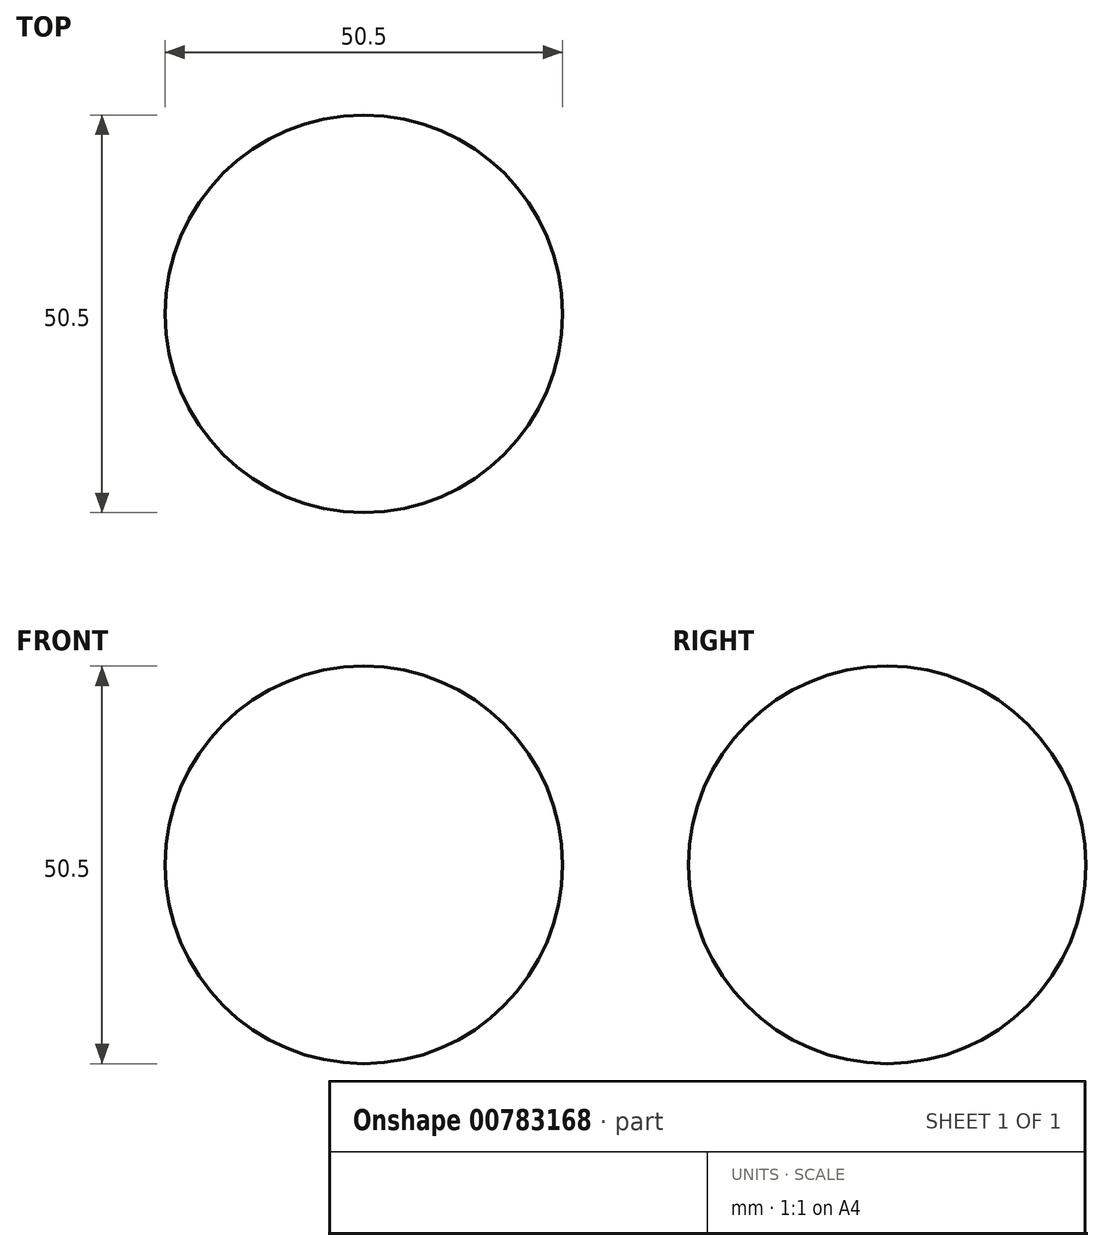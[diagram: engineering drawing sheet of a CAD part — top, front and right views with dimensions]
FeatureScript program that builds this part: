
annotation { "Feature Type Name" : "Feature", "Feature Type Description" : "" }
export const myFeature = defineFeature(function(context is Context, id is Id, definition is map)
    precondition{}
    {
        {
            var Q0;
            Q0=qCreatedBy(makeId("Front.planeOp"),FACE);
            var sketch = newSketch(context, id + "F0", { "sketchPlane" : qUnion([Q0])});
            skArc(sketch, "E0", {"start": v(0, -25.25) * mm, "mid": v(25.25, 0) * mm, "end": v(0, 25.25) * mm});
            skLineSegment(sketch, "E1", {"start": v(0, 25.25) * mm, "end": v(0, -25.25) * mm});
            skSolve(sketch);
        }
        {
            var Q0;
            Q0=makeQuery(id+"F0.imprint","IMPRINT",FACE,{"disambiguationData":[TD([[makeQuery(id+"F0.imprint","IMPRINT",EDGE,{"derivedFrom":sQuery(id+"F0.wireOp",EDGE,"E0")}),1.0]])]});
            var Q1;
            Q1=sQuery(id+"F0.wireOp",EDGE,"E1");
            revolve(context, id + "F1", {"surfaceOperationType" : NewSurfaceOperationType.NEW, "entities" : qUnion([Q0]), "axis" : qUnion([Q1]), "revolveType" : RevolveType.FULL});
        }
    });
